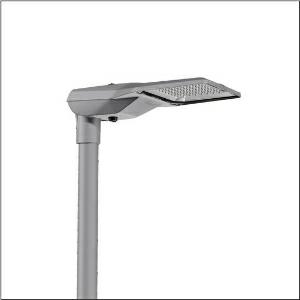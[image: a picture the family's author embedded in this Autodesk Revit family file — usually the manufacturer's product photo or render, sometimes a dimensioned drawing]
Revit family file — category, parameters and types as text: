
# Revit family: streetlight_sl_21_midi___stw1_0a_5xe3e43t08mb_20e1
name_source: partatom
category: Lighting Fixtures
units: mm (PartAtom-declared; Revit-internal decimal feet)

## family parameters
Cut with Voids When Loaded = No
Host = Face
Light Source = No
Part Type = Normal
Room Calculation Point = No
Round Connector Dimension = Use Diameter
Shared = No

## types (1)
- --- (1 x LED, 20180 lm, 147 W, 4000K)
    Apparent Load = 147 VA
    CIE Flux Codes = 38 75 98 100 100
    Color Rendering = 70
    Color Temperature = 4000K
    Default Elevation = 1800 mm
    Description = Streetlight SL 21 midi, mast luminaire, primary light control with lens, of PMMA, primary optical cover: cover, of toughened safety glass, transparent, light distribution: STW1.0a, light emission: direct distribution, primary light characteristic: asymmetric, installation type: side-entry, post-top, LED, High Power LED, rated luminous flux: 20.180lm, luminous efficacy: 137lm/W, light colour: 740, colour temperature: 4000K, control gear: D4i, control: overheat protection, constant luminous flux control, time-dependent luminous flux control, flexible luminous flux parameterisation, pre-setting: logarithmic dimming characteristic, mains connection: 230..240V, AC, 50/60Hz, start of lifetime: 147W, end of service life: 155W, reduction: 65W, luminaire housing, of diecast aluminium, powder-coated, SITECO metallic grey (DB 702S), corrosivity category C5 high according to DIN EN ISO 12944, please order mast flange separately, inclination adjustable: 0°, 5°, 10°, 15°, sealing non-destructively replaceable, multi-level sealing system, length: 644mm, width: 335mm, height: 110mm, mast flange for spigot size: 42mm (side-entry): 5XC10008XM4, 60/48mm (side-entry/post-top): 5XC10108XM2, 76/60mm (side-entry/post-top): 5XC10108XM1, mounting height: 4..8m, Smart Interface below and above, protection rating (complete): IP66, insulation class (complete): insulation class II (safety insulation), certification: CE, ENEC, ENEC+, VDE, impact resistance: IK10, permissible operating ambient temperature for outdoor applications: -40..+50°C, standard-compliant lighting for roads and squares, packaging unit: 1 piece

Light Distribution: STW1.0a
    Height = 111 mm
    Lamp = 1 x LED
    Lamp Light Flux = 20180 lm
    Lamp Power = 147 W
    Lamp count = 1
    Length = 644 mm
    Luminous efficacy = 137 lm/W
    Manufacturer = Siteco
    ModVariant = No
    Model = 5XE3E43T08MB
    Number of Poles = 1
    OnlyDefault = Yes
    Power Factor = 1
    Product Name = Streetlight SL 21 midi | STW1.0a
    Product group = mast luminaire | pylon top
    ProductGroupID = 6100
    Protection Class = Protection class II
    Protection Degree = IP 66
    RLX_Detail_Level = 1
    RLX_Emergency_Light_Flux = 0 lm
    RLX_Emergency_Type = 0
    RLX_Emergency_Type_DB = No
    RlxData = <blob elided: 27057 chars, md5=a9d4360c>
    Socket = socket
    Standby Power = 0 W
    System Light Flux = 20180 lm
    System Power = 147 W
    Type Comments = factory setting: luminous flux: 100 % | dim-lin: 254 | 750 mA
    Type Image = l_1004304.jpg
    URL = http://relux.com
    VarID = @adj_185335
    Voltage = 0 V
    Weight = 0.00 kg
    Width = 336 mm

## geometry (parser evidence)
native form markers: Blend x4, Sweep x11
no freeform markers — native parametric forms only
